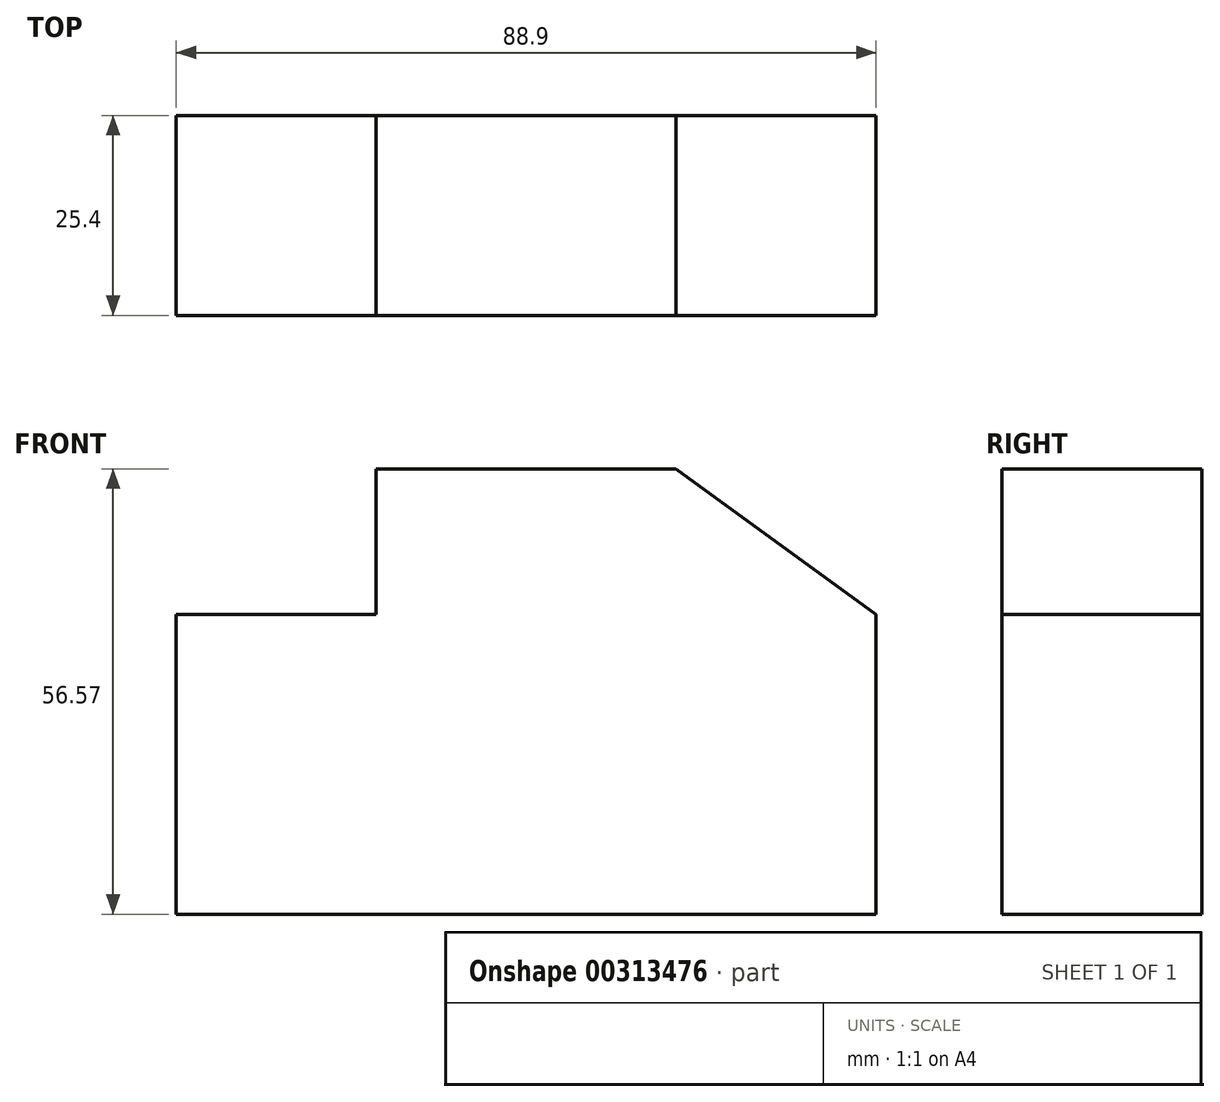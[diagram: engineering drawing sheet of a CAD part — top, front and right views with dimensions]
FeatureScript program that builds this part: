
annotation { "Feature Type Name" : "Feature", "Feature Type Description" : "" }
export const myFeature = defineFeature(function(context is Context, id is Id, definition is map)
    precondition{}
    {
        {
            var Q0;
            Q0=qCreatedBy(makeId("Front.planeOp"),FACE);
            var sketch = newSketch(context, id + "F0", { "sketchPlane" : qUnion([Q0])});
            skLineSegment(sketch, "E0", {"start": v(-46.61, 21.97) * mm, "end": v(-46.61, -16.13) * mm});
            skLineSegment(sketch, "E1", {"start": v(-46.61, -16.13) * mm, "end": v(42.29, -16.13) * mm});
            skLineSegment(sketch, "E2", {"start": v(42.29, -16.13) * mm, "end": v(42.29, 21.97) * mm});
            skLineSegment(sketch, "E3", {"start": v(-46.61, 21.97) * mm, "end": v(-21.21, 21.97) * mm});
            skLineSegment(sketch, "E4", {"start": v(-21.21, 21.97) * mm, "end": v(-21.21, 40.44) * mm});
            skLineSegment(sketch, "E5", {"start": v(-21.21, 40.44) * mm, "end": v(16.89, 40.44) * mm});
            skLineSegment(sketch, "E6", {"start": v(16.89, 40.44) * mm, "end": v(42.29, 21.97) * mm});
            skSolve(sketch);
        }
        {
            var Q0;
            Q0=makeQuery(id+"F0.imprint","IMPRINT",FACE,{"disambiguationData":[TD([[makeQuery(id+"F0.imprint","IMPRINT",EDGE,{"derivedFrom":sQuery(id+"F0.wireOp",EDGE,"E0")}),1.0]])]});
            extrude(context, id + "F1", {"entities" : qUnion([Q0]), "depth" : 25.4 * mm});
        }
    });
